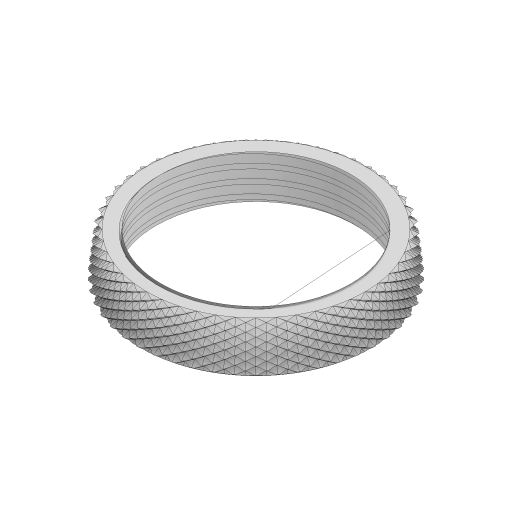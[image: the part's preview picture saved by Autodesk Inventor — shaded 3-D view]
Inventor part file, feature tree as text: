
AUTODESK INVENTOR PART (.ipt)
format: ipt  version: 2023 (Build 270158000, 158)  size: 9,543,168 bytes
history: native  units: mm
features: sketch x5, helix x3, draft x2, extrude x1, pattern_circular x1, mirror x1, revolve x1, projected_geometry x1
ambient origin geometry x8: Origin, YZ Plane, XZ Plane, XY Plane, X Axis, Y Axis, Z Axis, Center Point
bodies: Solid1 (feature_tree)
feature tree (15):
  extrude  "Extrusion1"  Depth=6.52mm TaperAngle=0.0deg
  draft  "FaceDraft1"
  sketch  "Sketch2"  dims[d7=2.0mm d8=9.0mm d9=10.0mm d10=1.047198mm d11=90.0deg d12=90.0deg d13=0.0mm d14=0.0mm d15=2.0mm d16=3.0mm d17=10.0mm d18=-1.047198mm d19=90.0deg d20=90.0deg d21=0.0mm d22=0.0mm d23=3.5mm d91=1.047198mm d109=1.308997mm]
  sketch  "Sketch4"  dims[d112=2.0mm d113=6.52mm d114=1.25mm d115=1.047198mm]
  helix  "Coil1"  [1 undecoded]
  helix  "Coil2"  [1 undecoded]
  draft  "FaceDraft2"
  helix  "Coil10"  [1 undecoded]
  pattern_circular  "Circular Pattern5"  Count=48 Angle=360.0deg
  mirror  "Mirror1"
  revolve  "Revolution2"  [1 undecoded]
  sketch  "Sketch1"  dims[d0=26.5mm d2=6.52mm d3=0.0mm d4=1.047198mm]
  sketch  "Sketch13"  dims[d116=90.0deg d117=90.0deg d118=0.0mm d119=0.0mm d122=480.0mm d123=360.0deg]
  sketch  "Sketch14"  dims[d127=60.0deg d128=15.211695mm d129=360.0deg d130=8.726646mm]
  projected_geometry  "Project Cut Edges1"
note: 4 required parameter values undecoded (feature->parameter linkage not recoverable at this tier; creation-order binding heuristic only, values carry confidence <= 0.55)